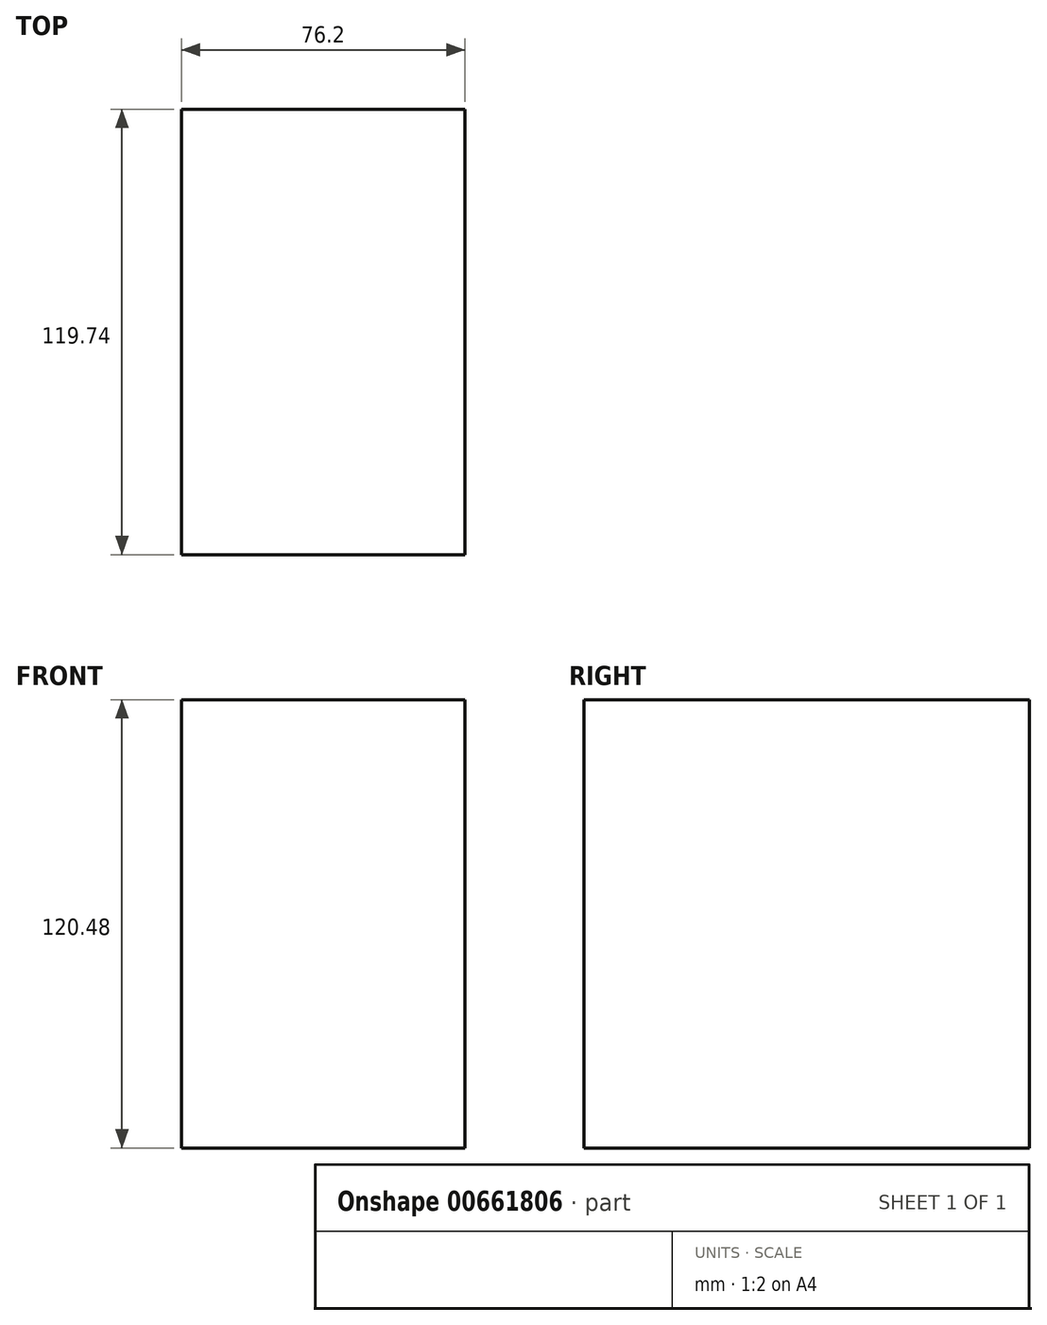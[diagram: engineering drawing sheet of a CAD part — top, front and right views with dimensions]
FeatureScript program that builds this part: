
annotation { "Feature Type Name" : "Feature", "Feature Type Description" : "" }
export const myFeature = defineFeature(function(context is Context, id is Id, definition is map)
    precondition{}
    {
        {
            var Q0;
            Q0=qCreatedBy(makeId("Right.planeOp"),FACE);
            var sketch = newSketch(context, id + "F0", { "sketchPlane" : qUnion([Q0])});
            skLineSegment(sketch, "E0.bottom", {"start": v(59.87, -60.24) * mm, "end": v(-59.87, -60.24) * mm});
            skLineSegment(sketch, "E0.top", {"start": v(59.87, 60.24) * mm, "end": v(-59.87, 60.24) * mm});
            skLineSegment(sketch, "E0.left", {"start": v(59.87, -60.24) * mm, "end": v(59.87, 60.24) * mm});
            skLineSegment(sketch, "E0.right", {"start": v(-59.87, -60.24) * mm, "end": v(-59.87, 60.24) * mm});
            skPoint(sketch, "E0.middle", {"position": v(0, 0) * mm});
            skSolve(sketch);
        }
        {
            var Q0;
            Q0=makeQuery(id+"F0.imprint","IMPRINT",FACE,{"disambiguationData":[TD([[makeQuery(id+"F0.imprint","IMPRINT",EDGE,{"derivedFrom":sQuery(id+"F0.wireOp",EDGE,"E0.bottom")}),-1.0]])]});
            extrude(context, id + "F1", {"entities" : qUnion([Q0]), "depth" : 76.2 * mm, "offsetDistance" : 25.4 * mm});
        }
    });
